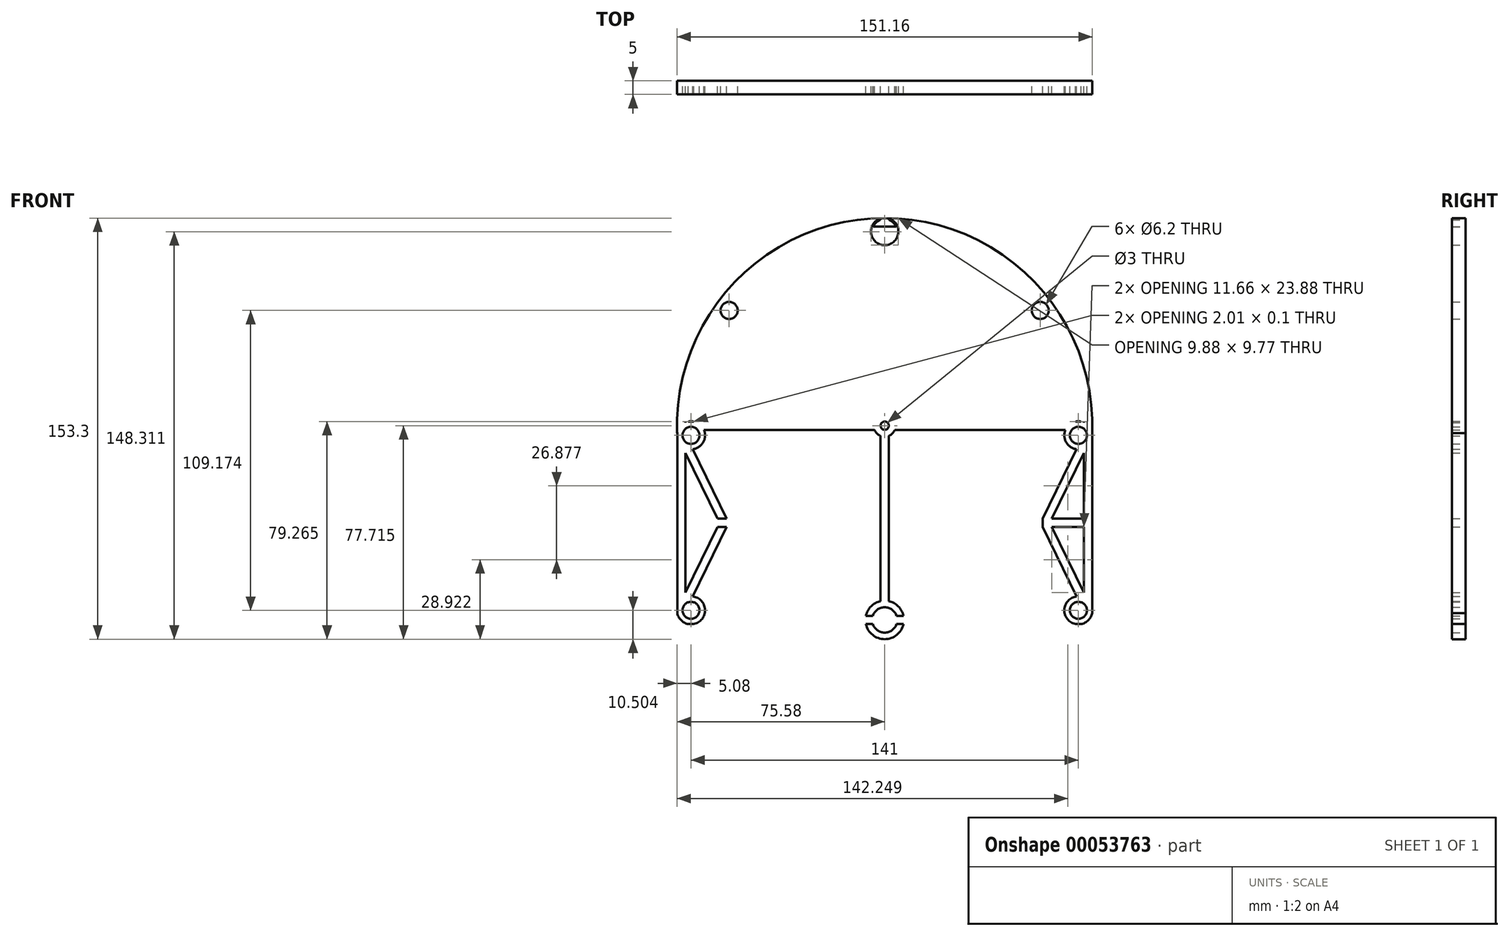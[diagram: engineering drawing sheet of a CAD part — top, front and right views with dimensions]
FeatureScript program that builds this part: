
annotation { "Feature Type Name" : "Feature", "Feature Type Description" : "" }
export const myFeature = defineFeature(function(context is Context, id is Id, definition is map)
    precondition{}
    {
        {
            var Q0;
            Q0=qCreatedBy(makeId("Front.planeOp"),FACE);
            var sketch = newSketch(context, id + "F0", { "sketchPlane" : qUnion([Q0])});
            skPoint(sketch, "E0", {"position": v(-3.58, 32.7) * mm});
            skPoint(sketch, "E1", {"position": v(-3.58, -38) * mm});
            skLineSegment(sketch, "E2.bottom", {"start": v(-5.08, 122.7) * mm, "end": v(-2.08, 122.7) * mm});
            skLineSegment(sketch, "E2.top", {"start": v(-5.08, -57.3) * mm, "end": v(-2.08, -57.3) * mm});
            skLineSegment(sketch, "E2.left", {"start": v(-5.08, 122.7) * mm, "end": v(-5.08, -57.3) * mm});
            skLineSegment(sketch, "E2.right", {"start": v(-2.08, 122.7) * mm, "end": v(-2.08, -57.3) * mm});
            skLineSegment(sketch, "E3", {"start": v(-3.58, 122.7) * mm, "end": v(-3.58, -57.3) * mm, "construction": true});
            skCircle(sketch, "E4", {"center": v(-3.58, 32.7) * mm, "radius": 1.5 * mm});
            skCircle(sketch, "E5", {"center": v(-3.58, -38) * mm, "radius": 1.5 * mm});
            skCircle(sketch, "E6", {"center": v(-3.58, 32.7) * mm, "radius": 4 * mm});
            skCircle(sketch, "E7", {"center": v(-3.58, -38) * mm, "radius": 7 * mm});
            skCircle(sketch, "E8", {"center": v(-3.58, 103.42) * mm, "radius": 4.5 * mm});
            skCircle(sketch, "E9", {"center": v(-3.58, 103.42) * mm, "radius": 5 * mm});
            skLineSegment(sketch, "E10.bottom", {"start": v(-76.08, -36.5) * mm, "end": v(68.92, -36.5) * mm});
            skLineSegment(sketch, "E10.top", {"start": v(-76.08, -39.5) * mm, "end": v(68.92, -39.5) * mm});
            skLineSegment(sketch, "E10.left", {"start": v(-76.08, -36.5) * mm, "end": v(-76.08, -39.5) * mm});
            skLineSegment(sketch, "E10.right", {"start": v(68.92, -36.5) * mm, "end": v(68.92, -39.5) * mm});
            skPoint(sketch, "E11", {"position": v(-3.58, -36.5) * mm});
            skPoint(sketch, "E12", {"position": v(-3.58, 34.2) * mm});
            skLineSegment(sketch, "E13.bottom", {"start": v(-76.08, 34.2) * mm, "end": v(68.92, 34.2) * mm});
            skLineSegment(sketch, "E13.top", {"start": v(-76.08, 31.2) * mm, "end": v(68.92, 31.2) * mm});
            skLineSegment(sketch, "E13.right", {"start": v(68.92, 34.2) * mm, "end": v(68.92, 31.2) * mm});
            skLineSegment(sketch, "E13.left", {"start": v(-76.08, 34.2) * mm, "end": v(-76.08, 31.2) * mm});
            skLineSegment(sketch, "E14.bottom", {"start": v(68.92, 34.2) * mm, "end": v(71.92, 34.2) * mm});
            skLineSegment(sketch, "E14.top", {"start": v(68.92, -39.5) * mm, "end": v(71.92, -39.5) * mm});
            skLineSegment(sketch, "E14.left", {"start": v(68.92, 34.2) * mm, "end": v(68.92, -39.5) * mm});
            skLineSegment(sketch, "E14.right", {"start": v(71.92, 34.2) * mm, "end": v(71.92, -39.5) * mm});
            skLineSegment(sketch, "E15.bottom", {"start": v(-76.08, 34.2) * mm, "end": v(-79.08, 34.2) * mm});
            skLineSegment(sketch, "E15.top", {"start": v(-76.08, -39.5) * mm, "end": v(-79.08, -39.5) * mm});
            skLineSegment(sketch, "E15.left", {"start": v(-76.08, 34.2) * mm, "end": v(-76.08, -39.5) * mm});
            skLineSegment(sketch, "E15.right", {"start": v(-79.08, 34.2) * mm, "end": v(-79.08, -39.5) * mm});
            skLineSegment(sketch, "E16", {"start": v(66.92, 34.2) * mm, "end": v(66.92, 29.2) * mm, "construction": true});
            skCircle(sketch, "E17", {"center": v(-3.58, -38) * mm, "radius": 64 * mm, "construction": true});
            skCircle(sketch, "E18", {"center": v(-3.58, 32.7) * mm, "radius": 64 * mm, "construction": true});
            skCircle(sketch, "E19", {"center": v(66.92, 29.2) * mm, "radius": 5.1 * mm});
            skCircle(sketch, "E20", {"center": v(66.92, 29.2) * mm, "radius": 3.1 * mm});
            skCircle(sketch, "E21", {"center": v(-3.58, -38) * mm, "radius": 4.6 * mm});
            skCircle(sketch, "E22.0.1.0", {"center": v(66.92, -34.5) * mm, "radius": 5.1 * mm});
            skCircle(sketch, "E22.0.1.2", {"center": v(66.92, -34.5) * mm, "radius": 3.1 * mm});
            skCircle(sketch, "E22.1.0.0", {"center": v(-74.08, 29.2) * mm, "radius": 5.1 * mm});
            skCircle(sketch, "E22.1.0.2", {"center": v(-74.08, 29.2) * mm, "radius": 3.1 * mm});
            skCircle(sketch, "E22.1.1.0", {"center": v(-74.08, -34.5) * mm, "radius": 5.1 * mm});
            skCircle(sketch, "E22.1.1.2", {"center": v(-74.08, -34.5) * mm, "radius": 3.1 * mm});
            skLineSegment(sketch, "E22.direction1", {"start": v(66.92, 29.2) * mm, "end": v(-74.08, 29.2) * mm, "construction": true});
            skLineSegment(sketch, "E22.direction2", {"start": v(66.92, 29.2) * mm, "end": v(66.92, -34.5) * mm, "construction": true});
            skArc(sketch, "E23", {"start": v(71.92, 29.2) * mm, "mid": v(-3.58, 108.29) * mm, "end": v(-79.08, 29.2) * mm});
            skArc(sketch, "E24", {"start": v(68.92, 33.79) * mm, "mid": v(-3.58, 105.21) * mm, "end": v(-76.08, 33.79) * mm});
            skLineSegment(sketch, "E25", {"start": v(-64.3, 77.7) * mm, "end": v(57.14, 77.7) * mm, "construction": true});
            skLineSegment(sketch, "E26", {"start": v(-64.3, 77.7) * mm, "end": v(-60.2, 74.67) * mm, "construction": true});
            skCircle(sketch, "E27", {"center": v(-60.2, 74.67) * mm, "radius": 5.1 * mm});
            skCircle(sketch, "E28", {"center": v(-60.2, 74.67) * mm, "radius": 3.1 * mm});
            skCircle(sketch, "E29.MirrorC", {"center": v(53.05, 74.67) * mm, "radius": 5.1 * mm});
            skCircle(sketch, "E30.MirrorC", {"center": v(53.05, 74.67) * mm, "radius": 3.1 * mm});
            skLineSegment(sketch, "E31", {"start": v(-79.08, -2.65) * mm, "end": v(71.92, -2.65) * mm, "construction": true});
            skLineSegment(sketch, "E32.bottom", {"start": v(-76.08, -1.15) * mm, "end": v(-61.08, -1.15) * mm});
            skLineSegment(sketch, "E32.top", {"start": v(-76.08, -4.15) * mm, "end": v(-61.08, -4.15) * mm});
            skLineSegment(sketch, "E32.left", {"start": v(-76.08, -1.15) * mm, "end": v(-76.08, -4.15) * mm});
            skLineSegment(sketch, "E32.right", {"start": v(-61.08, -1.15) * mm, "end": v(-61.08, -4.15) * mm});
            skPoint(sketch, "E33", {"position": v(-76.08, -2.65) * mm});
            skLineSegment(sketch, "E34", {"start": v(-61.08, -2.65) * mm, "end": v(-79.08, 34.2) * mm, "construction": true});
            skLineSegment(sketch, "E35", {"start": v(-61.08, -2.65) * mm, "end": v(-79.08, -39.5) * mm, "construction": true});
            skLineSegment(sketch, "E36", {"start": v(-61.08, -1.15) * mm, "end": v(-73.44, 24.15) * mm});
            skLineSegment(sketch, "E37", {"start": v(-76.08, 22.73) * mm, "end": v(-64.42, -1.15) * mm});
            skLineSegment(sketch, "E38", {"start": v(-61.08, -4.15) * mm, "end": v(-73.44, -29.45) * mm});
            skLineSegment(sketch, "E39", {"start": v(-64.42, -4.15) * mm, "end": v(-76.08, -28.03) * mm});
            skLineSegment(sketch, "E40.MirrorCS", {"start": v(68.92, -1.15) * mm, "end": v(53.92, -1.15) * mm});
            skLineSegment(sketch, "E41.MirrorCS", {"start": v(68.92, -4.15) * mm, "end": v(53.92, -4.15) * mm});
            skLineSegment(sketch, "E42.MirrorCS", {"start": v(53.92, -1.15) * mm, "end": v(53.92, -4.15) * mm});
            skLineSegment(sketch, "E43.MirrorCS", {"start": v(53.92, -1.15) * mm, "end": v(66.27, 24.15) * mm});
            skLineSegment(sketch, "E44.MirrorCS", {"start": v(68.92, 22.73) * mm, "end": v(57.26, -1.15) * mm});
            skLineSegment(sketch, "E45.MirrorCS", {"start": v(53.92, -4.15) * mm, "end": v(66.27, -29.45) * mm});
            skLineSegment(sketch, "E46.MirrorCS", {"start": v(57.26, -4.15) * mm, "end": v(68.92, -28.03) * mm});
            skSolve(sketch);
        }
        {
            var Q0;
            {var subQ0=sQuery(id+"F0.wireOp",EDGE,"E4");var subQ1=sQuery(id+"F0.wireOp",EDGE,"E2.left");var subQ2=makeQuery(id+"F0.imprint","INTERSECT",VERTEX,{"derivedFrom":[subQ1,subQ0]});Q0=makeQuery(id+"F0.imprint","IMPRINT",FACE,{"disambiguationData":[TD([[makeQuery(id+"F0.imprint","IMPRINT",EDGE,{"disambiguationData":[TD([[subQ2,-1.0]])],"derivedFrom":subQ1}),1.0]])]});}
            var Q1;
            {var subQ0=sQuery(id+"F0.wireOp",EDGE,"E4");var subQ1=sQuery(id+"F0.wireOp",EDGE,"E2.right");var subQ2=makeQuery(id+"F0.imprint","INTERSECT",VERTEX,{"derivedFrom":[subQ1,subQ0]});Q1=makeQuery(id+"F0.imprint","IMPRINT",FACE,{"disambiguationData":[TD([[makeQuery(id+"F0.imprint","IMPRINT",EDGE,{"disambiguationData":[TD([[subQ2,-1.0]])],"derivedFrom":subQ1}),-1.0]])]});}
            var Q2;
            {var subQ0=sQuery(id+"F0.wireOp",EDGE,"E13.bottom");var subQ3=sQuery(id+"F0.wireOp",EDGE,"E2.left");var subQ4=makeQuery(id+"F0.imprint","INTERSECT",VERTEX,{"derivedFrom":[subQ3,subQ0]});Q2=makeQuery(id+"F0.imprint","IMPRINT",FACE,{"disambiguationData":[TD([[makeQuery(id+"F0.imprint","IMPRINT",EDGE,{"disambiguationData":[TD([[subQ4,-1.0]])],"derivedFrom":subQ3}),-1.0]])]});}
            var Q3;
            {var subQ0=sQuery(id+"F0.wireOp",EDGE,"E13.bottom");var subQ3=sQuery(id+"F0.wireOp",EDGE,"E2.right");var subQ4=makeQuery(id+"F0.imprint","INTERSECT",VERTEX,{"derivedFrom":[subQ3,subQ0]});Q3=makeQuery(id+"F0.imprint","IMPRINT",FACE,{"disambiguationData":[TD([[makeQuery(id+"F0.imprint","IMPRINT",EDGE,{"disambiguationData":[TD([[subQ4,-1.0]])],"derivedFrom":subQ3}),1.0]])]});}
            var Q4;
            {var subQ0=sQuery(id+"F0.wireOp",EDGE,"E13.bottom");var subQ1=sQuery(id+"F0.wireOp",EDGE,"E2.right");var subQ2=makeQuery(id+"F0.imprint","INTERSECT",VERTEX,{"derivedFrom":[subQ1,subQ0]});Q4=makeQuery(id+"F0.imprint","IMPRINT",FACE,{"disambiguationData":[TD([[makeQuery(id+"F0.imprint","IMPRINT",EDGE,{"disambiguationData":[TD([[subQ2,-1.0]])],"derivedFrom":subQ1}),-1.0]])]});}
            var Q5;
            {var subQ0=sQuery(id+"F0.wireOp",EDGE,"E13.bottom");var subQ1=sQuery(id+"F0.wireOp",EDGE,"E2.left");var subQ2=makeQuery(id+"F0.imprint","INTERSECT",VERTEX,{"derivedFrom":[subQ1,subQ0]});Q5=makeQuery(id+"F0.imprint","IMPRINT",FACE,{"disambiguationData":[TD([[makeQuery(id+"F0.imprint","IMPRINT",EDGE,{"disambiguationData":[TD([[subQ2,-1.0]])],"derivedFrom":subQ1}),1.0]])]});}
            var Q6;
            {var subQ0=sQuery(id+"F0.wireOp",EDGE,"E13.top");var subQ1=sQuery(id+"F0.wireOp",EDGE,"E2.left");var subQ2=makeQuery(id+"F0.imprint","INTERSECT",VERTEX,{"derivedFrom":[subQ1,subQ0]});Q6=makeQuery(id+"F0.imprint","IMPRINT",FACE,{"disambiguationData":[TD([[makeQuery(id+"F0.imprint","IMPRINT",EDGE,{"disambiguationData":[TD([[subQ2,-1.0]])],"derivedFrom":subQ1}),1.0]])]});}
            var Q7;
            {var subQ0=sQuery(id+"F0.wireOp",EDGE,"E13.top");var subQ1=sQuery(id+"F0.wireOp",EDGE,"E2.left");var subQ2=makeQuery(id+"F0.imprint","INTERSECT",VERTEX,{"derivedFrom":[subQ1,subQ0]});Q7=makeQuery(id+"F0.imprint","IMPRINT",FACE,{"disambiguationData":[TD([[makeQuery(id+"F0.imprint","IMPRINT",EDGE,{"disambiguationData":[TD([[subQ2,-1.0]])],"derivedFrom":subQ1}),1.0]])]});}
            var Q8;
            {var subQ0=sQuery(id+"F0.wireOp",EDGE,"E22.1.0.2");var subQ1=sQuery(id+"F0.wireOp",EDGE,"E15.left");var subQ2=makeQuery(id+"F0.imprint","INTERSECT",VERTEX,{"disambiguationData":[OD(1.0)],"derivedFrom":[subQ1,subQ0]});Q8=makeQuery(id+"F0.imprint","IMPRINT",FACE,{"disambiguationData":[TD([[makeQuery(id+"F0.imprint","IMPRINT",EDGE,{"disambiguationData":[TD([[subQ2,-1.0]])],"derivedFrom":subQ1}),-1.0]])]});}
            var Q9;
            {var subQ0=sQuery(id+"F0.wireOp",EDGE,"E19");var subQ1=sQuery(id+"F0.wireOp",EDGE,"E14.left");var subQ2=makeQuery(id+"F0.imprint","INTERSECT",VERTEX,{"derivedFrom":[subQ1,subQ0]});Q9=makeQuery(id+"F0.imprint","IMPRINT",FACE,{"disambiguationData":[TD([[makeQuery(id+"F0.imprint","IMPRINT",EDGE,{"disambiguationData":[TD([[subQ2,-1.0]])],"derivedFrom":subQ1}),1.0]])]});}
            var Q10;
            {var subQ0=sQuery(id+"F0.wireOp",EDGE,"E19");var subQ1=sQuery(id+"F0.wireOp",EDGE,"E14.left");var subQ2=makeQuery(id+"F0.imprint","INTERSECT",VERTEX,{"derivedFrom":[subQ1,subQ0]});Q10=makeQuery(id+"F0.imprint","IMPRINT",FACE,{"disambiguationData":[TD([[makeQuery(id+"F0.imprint","IMPRINT",EDGE,{"disambiguationData":[TD([[subQ2,-1.0]])],"derivedFrom":subQ1}),1.0]])]});}
            var Q11;
            {var subQ0=sQuery(id+"F0.wireOp",EDGE,"E19");var subQ1=sQuery(id+"F0.wireOp",EDGE,"E13.top");var subQ2=makeQuery(id+"F0.imprint","INTERSECT",VERTEX,{"derivedFrom":[subQ1,subQ0]});Q11=makeQuery(id+"F0.imprint","IMPRINT",FACE,{"disambiguationData":[TD([[makeQuery(id+"F0.imprint","IMPRINT",EDGE,{"disambiguationData":[TD([[subQ2,-1.0]])],"derivedFrom":subQ1}),-1.0]])]});}
            var Q12;
            {var subQ0=sQuery(id+"F0.wireOp",EDGE,"E19");var subQ3=sQuery(id+"F0.wireOp",EDGE,"E13.top");var subQ4=makeQuery(id+"F0.imprint","INTERSECT",VERTEX,{"derivedFrom":[subQ3,subQ0]});Q12=makeQuery(id+"F0.imprint","IMPRINT",FACE,{"disambiguationData":[TD([[makeQuery(id+"F0.imprint","IMPRINT",EDGE,{"disambiguationData":[TD([[subQ4,-1.0]])],"derivedFrom":subQ3}),1.0]])]});}
            var Q13;
            {var subQ0=sQuery(id+"F0.wireOp",EDGE,"E13.bottom");var subQ1=sQuery(id+"F0.wireOp",EDGE,"E6");var subQ2=makeQuery(id+"F0.imprint","INTERSECT",VERTEX,{"disambiguationData":[OD(1.0)],"derivedFrom":[subQ1,subQ0]});Q13=makeQuery(id+"F0.imprint","IMPRINT",FACE,{"disambiguationData":[TD([[makeQuery(id+"F0.imprint","IMPRINT",EDGE,{"disambiguationData":[TD([[subQ2,-1.0]])],"derivedFrom":subQ1}),-1.0]])]});}
            var Q14;
            {var subQ0=sQuery(id+"F0.wireOp",EDGE,"E13.bottom");var subQ1=sQuery(id+"F0.wireOp",EDGE,"E6");var subQ2=makeQuery(id+"F0.imprint","INTERSECT",VERTEX,{"disambiguationData":[OD(0.0)],"derivedFrom":[subQ1,subQ0]});Q14=makeQuery(id+"F0.imprint","IMPRINT",FACE,{"disambiguationData":[TD([[makeQuery(id+"F0.imprint","IMPRINT",EDGE,{"disambiguationData":[TD([[subQ2,1.0]])],"derivedFrom":subQ1}),-1.0]])]});}
            var Q15;
            {var subQ0=sQuery(id+"F0.wireOp",EDGE,"E10.top");var subQ1=sQuery(id+"F0.wireOp",EDGE,"E7");var subQ2=makeQuery(id+"F0.imprint","INTERSECT",VERTEX,{"disambiguationData":[OD(1.0)],"derivedFrom":[subQ1,subQ0]});Q15=makeQuery(id+"F0.imprint","IMPRINT",FACE,{"disambiguationData":[TD([[makeQuery(id+"F0.imprint","IMPRINT",EDGE,{"disambiguationData":[TD([[subQ2,-1.0]])],"derivedFrom":subQ1}),-1.0]])]});}
            var Q16;
            {var subQ0=sQuery(id+"F0.wireOp",EDGE,"E10.top");var subQ1=sQuery(id+"F0.wireOp",EDGE,"E7");var subQ2=makeQuery(id+"F0.imprint","INTERSECT",VERTEX,{"disambiguationData":[OD(0.0)],"derivedFrom":[subQ1,subQ0]});Q16=makeQuery(id+"F0.imprint","IMPRINT",FACE,{"disambiguationData":[TD([[makeQuery(id+"F0.imprint","IMPRINT",EDGE,{"disambiguationData":[TD([[subQ2,1.0]])],"derivedFrom":subQ1}),-1.0]])]});}
            var Q17;
            {var subQ0=sQuery(id+"F0.wireOp",EDGE,"E13.top");var subQ1=sQuery(id+"F0.wireOp",EDGE,"E2.right");var subQ2=makeQuery(id+"F0.imprint","INTERSECT",VERTEX,{"derivedFrom":[subQ1,subQ0]});Q17=makeQuery(id+"F0.imprint","IMPRINT",FACE,{"disambiguationData":[TD([[makeQuery(id+"F0.imprint","IMPRINT",EDGE,{"disambiguationData":[TD([[subQ2,-1.0]])],"derivedFrom":subQ1}),1.0]])]});}
            var Q18;
            {var subQ0=sQuery(id+"F0.wireOp",EDGE,"E13.top");var subQ1=sQuery(id+"F0.wireOp",EDGE,"E2.left");var subQ2=makeQuery(id+"F0.imprint","INTERSECT",VERTEX,{"derivedFrom":[subQ1,subQ0]});Q18=makeQuery(id+"F0.imprint","IMPRINT",FACE,{"disambiguationData":[TD([[makeQuery(id+"F0.imprint","IMPRINT",EDGE,{"disambiguationData":[TD([[subQ2,-1.0]])],"derivedFrom":subQ1}),-1.0]])]});}
            var Q19;
            {var subQ1=sQuery(id+"F0.wireOp",EDGE,"E2.left");var subQ4=sQuery(id+"F0.wireOp",EDGE,"E6");var subQ5=makeQuery(id+"F0.imprint","INTERSECT",VERTEX,{"disambiguationData":[OD(0.0)],"derivedFrom":[subQ1,subQ4]});Q19=makeQuery(id+"F0.imprint","IMPRINT",FACE,{"disambiguationData":[TD([[makeQuery(id+"F0.imprint","IMPRINT",EDGE,{"disambiguationData":[TD([[subQ5,-1.0]])],"derivedFrom":subQ1}),1.0]])]});}
            var Q20;
            {var subQ0=sQuery(id+"F0.wireOp",EDGE,"E6");var subQ1=sQuery(id+"F0.wireOp",EDGE,"E2.right");var subQ2=makeQuery(id+"F0.imprint","INTERSECT",VERTEX,{"disambiguationData":[OD(0.0)],"derivedFrom":[subQ1,subQ0]});Q20=makeQuery(id+"F0.imprint","IMPRINT",FACE,{"disambiguationData":[TD([[makeQuery(id+"F0.imprint","IMPRINT",EDGE,{"disambiguationData":[TD([[subQ2,-1.0]])],"derivedFrom":subQ1}),1.0]])]});}
            var Q21;
            {var subQ0=sQuery(id+"F0.wireOp",EDGE,"E6");var subQ1=sQuery(id+"F0.wireOp",EDGE,"E2.left");var subQ2=makeQuery(id+"F0.imprint","INTERSECT",VERTEX,{"disambiguationData":[OD(0.0)],"derivedFrom":[subQ1,subQ0]});Q21=makeQuery(id+"F0.imprint","IMPRINT",FACE,{"disambiguationData":[TD([[makeQuery(id+"F0.imprint","IMPRINT",EDGE,{"disambiguationData":[TD([[subQ2,-1.0]])],"derivedFrom":subQ1}),-1.0]])]});}
            var Q22;
            {var subQ0=sQuery(id+"F0.wireOp",EDGE,"E4");var subQ1=sQuery(id+"F0.wireOp",EDGE,"E2.right");var subQ2=makeQuery(id+"F0.imprint","INTERSECT",VERTEX,{"derivedFrom":[subQ1,subQ0]});Q22=makeQuery(id+"F0.imprint","IMPRINT",FACE,{"disambiguationData":[TD([[makeQuery(id+"F0.imprint","IMPRINT",EDGE,{"disambiguationData":[TD([[subQ2,-1.0]])],"derivedFrom":subQ1}),-1.0]])]});}
            var Q23;
            {var subQ0=sQuery(id+"F0.wireOp",EDGE,"E4");var subQ1=sQuery(id+"F0.wireOp",EDGE,"E2.left");var subQ2=makeQuery(id+"F0.imprint","INTERSECT",VERTEX,{"derivedFrom":[subQ1,subQ0]});Q23=makeQuery(id+"F0.imprint","IMPRINT",FACE,{"disambiguationData":[TD([[makeQuery(id+"F0.imprint","IMPRINT",EDGE,{"disambiguationData":[TD([[subQ2,-1.0]])],"derivedFrom":subQ1}),1.0]])]});}
            var Q24;
            {var subQ0=sQuery(id+"F0.wireOp",EDGE,"E7");var subQ1=sQuery(id+"F0.wireOp",EDGE,"E2.left");var subQ2=makeQuery(id+"F0.imprint","INTERSECT",VERTEX,{"disambiguationData":[OD(0.0)],"derivedFrom":[subQ1,subQ0]});Q24=makeQuery(id+"F0.imprint","IMPRINT",FACE,{"disambiguationData":[TD([[makeQuery(id+"F0.imprint","IMPRINT",EDGE,{"disambiguationData":[TD([[subQ2,1.0]])],"derivedFrom":subQ1}),1.0]])]});}
            var Q25;
            {var subQ0=sQuery(id+"F0.wireOp",EDGE,"E7");var subQ1=sQuery(id+"F0.wireOp",EDGE,"E2.right");var subQ2=makeQuery(id+"F0.imprint","INTERSECT",VERTEX,{"disambiguationData":[OD(0.0)],"derivedFrom":[subQ1,subQ0]});Q25=makeQuery(id+"F0.imprint","IMPRINT",FACE,{"disambiguationData":[TD([[makeQuery(id+"F0.imprint","IMPRINT",EDGE,{"disambiguationData":[TD([[subQ2,1.0]])],"derivedFrom":subQ1}),1.0]])]});}
            var Q26;
            {var subQ0=sQuery(id+"F0.wireOp",EDGE,"E7");var subQ1=sQuery(id+"F0.wireOp",EDGE,"E2.left");var subQ2=makeQuery(id+"F0.imprint","INTERSECT",VERTEX,{"disambiguationData":[OD(0.0)],"derivedFrom":[subQ1,subQ0]});Q26=makeQuery(id+"F0.imprint","IMPRINT",FACE,{"disambiguationData":[TD([[makeQuery(id+"F0.imprint","IMPRINT",EDGE,{"disambiguationData":[TD([[subQ2,1.0]])],"derivedFrom":subQ1}),-1.0]])]});}
            var Q27;
            {var subQ0=sQuery(id+"F0.wireOp",EDGE,"E7");var subQ1=sQuery(id+"F0.wireOp",EDGE,"E2.left");var subQ2=makeQuery(id+"F0.imprint","INTERSECT",VERTEX,{"disambiguationData":[OD(1.0)],"derivedFrom":[subQ1,subQ0]});Q27=makeQuery(id+"F0.imprint","IMPRINT",FACE,{"disambiguationData":[TD([[makeQuery(id+"F0.imprint","IMPRINT",EDGE,{"disambiguationData":[TD([[subQ2,-1.0]])],"derivedFrom":subQ1}),-1.0]])]});}
            var Q28;
            {var subQ0=sQuery(id+"F0.wireOp",EDGE,"E7");var subQ1=sQuery(id+"F0.wireOp",EDGE,"E2.left");var subQ2=makeQuery(id+"F0.imprint","INTERSECT",VERTEX,{"disambiguationData":[OD(1.0)],"derivedFrom":[subQ1,subQ0]});Q28=makeQuery(id+"F0.imprint","IMPRINT",FACE,{"disambiguationData":[TD([[makeQuery(id+"F0.imprint","IMPRINT",EDGE,{"disambiguationData":[TD([[subQ2,-1.0]])],"derivedFrom":subQ1}),1.0]])]});}
            var Q29;
            {var subQ0=sQuery(id+"F0.wireOp",EDGE,"E7");var subQ1=sQuery(id+"F0.wireOp",EDGE,"E2.right");var subQ2=makeQuery(id+"F0.imprint","INTERSECT",VERTEX,{"disambiguationData":[OD(1.0)],"derivedFrom":[subQ1,subQ0]});Q29=makeQuery(id+"F0.imprint","IMPRINT",FACE,{"disambiguationData":[TD([[makeQuery(id+"F0.imprint","IMPRINT",EDGE,{"disambiguationData":[TD([[subQ2,-1.0]])],"derivedFrom":subQ1}),1.0]])]});}
            var Q30;
            {var subQ0=sQuery(id+"F0.wireOp",EDGE,"E10.top");var subQ1=sQuery(id+"F0.wireOp",EDGE,"E7");var subQ2=makeQuery(id+"F0.imprint","INTERSECT",VERTEX,{"disambiguationData":[OD(1.0)],"derivedFrom":[subQ1,subQ0]});Q30=makeQuery(id+"F0.imprint","IMPRINT",FACE,{"disambiguationData":[TD([[makeQuery(id+"F0.imprint","IMPRINT",EDGE,{"disambiguationData":[TD([[subQ2,-1.0]])],"derivedFrom":subQ1}),1.0]])]});}
            var Q31;
            {var subQ0=sQuery(id+"F0.wireOp",EDGE,"E10.top");var subQ1=sQuery(id+"F0.wireOp",EDGE,"E7");var subQ2=makeQuery(id+"F0.imprint","INTERSECT",VERTEX,{"disambiguationData":[OD(0.0)],"derivedFrom":[subQ1,subQ0]});Q31=makeQuery(id+"F0.imprint","IMPRINT",FACE,{"disambiguationData":[TD([[makeQuery(id+"F0.imprint","IMPRINT",EDGE,{"disambiguationData":[TD([[subQ2,1.0]])],"derivedFrom":subQ1}),1.0]])]});}
            var Q32;
            {var subQ4=sQuery(id+"F0.wireOp",EDGE,"E20");var subQ5=sQuery(id+"F0.wireOp",EDGE,"E14.left");var subQ6=makeQuery(id+"F0.imprint","INTERSECT",VERTEX,{"disambiguationData":[OD(1.0)],"derivedFrom":[subQ5,subQ4]});Q32=makeQuery(id+"F0.imprint","IMPRINT",FACE,{"disambiguationData":[TD([[makeQuery(id+"F0.imprint","IMPRINT",EDGE,{"disambiguationData":[TD([[subQ6,-1.0]])],"derivedFrom":subQ5}),1.0]])]});}
            var Q33;
            {var subQ0=sQuery(id+"F0.wireOp",EDGE,"E22.0.1.0");var subQ3=sQuery(id+"F0.wireOp",EDGE,"E10.bottom");var subQ4=makeQuery(id+"F0.imprint","INTERSECT",VERTEX,{"derivedFrom":[subQ3,subQ0]});Q33=makeQuery(id+"F0.imprint","IMPRINT",FACE,{"disambiguationData":[TD([[makeQuery(id+"F0.imprint","IMPRINT",EDGE,{"disambiguationData":[TD([[subQ4,-1.0]])],"derivedFrom":subQ3}),-1.0]])]});}
            var Q34;
            {var subQ0=sQuery(id+"F0.wireOp",EDGE,"E22.0.1.0");var subQ1=sQuery(id+"F0.wireOp",EDGE,"E10.bottom");var subQ2=makeQuery(id+"F0.imprint","INTERSECT",VERTEX,{"derivedFrom":[subQ1,subQ0]});Q34=makeQuery(id+"F0.imprint","IMPRINT",FACE,{"disambiguationData":[TD([[makeQuery(id+"F0.imprint","IMPRINT",EDGE,{"disambiguationData":[TD([[subQ2,-1.0]])],"derivedFrom":subQ1}),1.0]])]});}
            var Q35;
            {var subQ0=sQuery(id+"F0.wireOp",EDGE,"E22.1.0.0");var subQ1=sQuery(id+"F0.wireOp",EDGE,"E15.left");var subQ2=makeQuery(id+"F0.imprint","INTERSECT",VERTEX,{"derivedFrom":[subQ1,subQ0]});Q35=makeQuery(id+"F0.imprint","IMPRINT",FACE,{"disambiguationData":[TD([[makeQuery(id+"F0.imprint","IMPRINT",EDGE,{"disambiguationData":[TD([[subQ2,-1.0]])],"derivedFrom":subQ1}),-1.0]])]});}
            var Q36;
            {var subQ3=sQuery(id+"F0.wireOp",EDGE,"E13.top");var subQ5=sQuery(id+"F0.wireOp",EDGE,"E22.1.0.2");var subQ6=makeQuery(id+"F0.imprint","INTERSECT",VERTEX,{"derivedFrom":[subQ3,subQ5]});Q36=makeQuery(id+"F0.imprint","IMPRINT",FACE,{"disambiguationData":[TD([[makeQuery(id+"F0.imprint","IMPRINT",EDGE,{"disambiguationData":[TD([[subQ6,-1.0]])],"derivedFrom":subQ3}),1.0]])]});}
            var Q37;
            {var subQ0=sQuery(id+"F0.wireOp",EDGE,"E22.1.0.2");var subQ1=sQuery(id+"F0.wireOp",EDGE,"E13.top");var subQ2=makeQuery(id+"F0.imprint","INTERSECT",VERTEX,{"derivedFrom":[subQ1,subQ0]});Q37=makeQuery(id+"F0.imprint","IMPRINT",FACE,{"disambiguationData":[TD([[makeQuery(id+"F0.imprint","IMPRINT",EDGE,{"disambiguationData":[TD([[subQ2,-1.0]])],"derivedFrom":subQ1}),-1.0]])]});}
            var Q38;
            {var subQ0=sQuery(id+"F0.wireOp",EDGE,"E22.1.1.2");var subQ1=sQuery(id+"F0.wireOp",EDGE,"E10.bottom");var subQ2=makeQuery(id+"F0.imprint","INTERSECT",VERTEX,{"derivedFrom":[subQ1,subQ0]});Q38=makeQuery(id+"F0.imprint","IMPRINT",FACE,{"disambiguationData":[TD([[makeQuery(id+"F0.imprint","IMPRINT",EDGE,{"disambiguationData":[TD([[subQ2,-1.0]])],"derivedFrom":subQ1}),1.0]])]});}
            var Q39;
            {var subQ5=sQuery(id+"F0.wireOp",EDGE,"E22.1.1.2");var subQ7=sQuery(id+"F0.wireOp",EDGE,"E10.bottom");var subQ9=makeQuery(id+"F0.imprint","INTERSECT",VERTEX,{"derivedFrom":[subQ7,subQ5]});Q39=makeQuery(id+"F0.imprint","IMPRINT",FACE,{"disambiguationData":[TD([[makeQuery(id+"F0.imprint","IMPRINT",EDGE,{"disambiguationData":[TD([[subQ9,-1.0]])],"derivedFrom":subQ7}),-1.0]])]});}
            var Q40;
            {var subQ0=sQuery(id+"F0.wireOp",EDGE,"E22.0.1.0");var subQ2=sQuery(id+"F0.wireOp",EDGE,"E14.left");var subQ4=makeQuery(id+"F0.imprint","INTERSECT",VERTEX,{"disambiguationData":[OD(0.0)],"derivedFrom":[subQ2,subQ0]});Q40=makeQuery(id+"F0.imprint","IMPRINT",FACE,{"disambiguationData":[TD([[makeQuery(id+"F0.imprint","IMPRINT",EDGE,{"disambiguationData":[TD([[subQ4,-1.0]])],"derivedFrom":subQ2}),1.0]])]});}
            var Q41;
            {var subQ0=sQuery(id+"F0.wireOp",EDGE,"E22.1.1.0");var subQ2=sQuery(id+"F0.wireOp",EDGE,"E15.left");var subQ4=makeQuery(id+"F0.imprint","INTERSECT",VERTEX,{"disambiguationData":[OD(0.0)],"derivedFrom":[subQ2,subQ0]});Q41=makeQuery(id+"F0.imprint","IMPRINT",FACE,{"disambiguationData":[TD([[makeQuery(id+"F0.imprint","IMPRINT",EDGE,{"disambiguationData":[TD([[subQ4,-1.0]])],"derivedFrom":subQ2}),-1.0]])]});}
            var Q42;
            {var subQ0=sQuery(id+"F0.wireOp",EDGE,"E15.bottom");Q42=makeQuery(id+"F0.imprint","IMPRINT",FACE,{"disambiguationData":[TD([[makeQuery(id+"F0.imprint","IMPRINT",EDGE,{"derivedFrom":subQ0}),-1.0]])]});}
            var Q43;
            {var subQ0=sQuery(id+"F0.wireOp",EDGE,"E14.bottom");Q43=makeQuery(id+"F0.imprint","IMPRINT",FACE,{"disambiguationData":[TD([[makeQuery(id+"F0.imprint","IMPRINT",EDGE,{"derivedFrom":subQ0}),1.0]])]});}
            var Q44;
            {var subQ0=sQuery(id+"F0.wireOp",EDGE,"E15.bottom");Q44=makeQuery(id+"F0.imprint","IMPRINT",FACE,{"disambiguationData":[TD([[makeQuery(id+"F0.imprint","IMPRINT",EDGE,{"derivedFrom":subQ0}),1.0]])]});}
            var Q45;
            {var subQ0=sQuery(id+"F0.wireOp",EDGE,"E14.bottom");Q45=makeQuery(id+"F0.imprint","IMPRINT",FACE,{"disambiguationData":[TD([[makeQuery(id+"F0.imprint","IMPRINT",EDGE,{"derivedFrom":subQ0}),-1.0]])]});}
            var Q46;
            {var subQ0=sQuery(id+"F0.wireOp",EDGE,"E9");var subQ1=sQuery(id+"F0.wireOp",EDGE,"E2.left");var subQ2=makeQuery(id+"F0.imprint","INTERSECT",VERTEX,{"disambiguationData":[OD(0.0)],"derivedFrom":[subQ1,subQ0]});Q46=makeQuery(id+"F0.imprint","IMPRINT",FACE,{"disambiguationData":[TD([[makeQuery(id+"F0.imprint","IMPRINT",EDGE,{"disambiguationData":[TD([[subQ2,-1.0]])],"derivedFrom":subQ1}),-1.0]])]});}
            var Q47;
            {var subQ0=sQuery(id+"F0.wireOp",EDGE,"E9");var subQ8=sQuery(id+"F0.wireOp",EDGE,"E2.left");var subQ10=makeQuery(id+"F0.imprint","INTERSECT",VERTEX,{"disambiguationData":[OD(0.0)],"derivedFrom":[subQ8,subQ0]});Q47=makeQuery(id+"F0.imprint","IMPRINT",FACE,{"disambiguationData":[TD([[makeQuery(id+"F0.imprint","IMPRINT",EDGE,{"disambiguationData":[TD([[subQ10,-1.0]])],"derivedFrom":subQ8}),1.0]])]});}
            var Q48;
            {var subQ0=sQuery(id+"F0.wireOp",EDGE,"E9");var subQ1=sQuery(id+"F0.wireOp",EDGE,"E2.right");var subQ2=makeQuery(id+"F0.imprint","INTERSECT",VERTEX,{"disambiguationData":[OD(0.0)],"derivedFrom":[subQ1,subQ0]});Q48=makeQuery(id+"F0.imprint","IMPRINT",FACE,{"disambiguationData":[TD([[makeQuery(id+"F0.imprint","IMPRINT",EDGE,{"disambiguationData":[TD([[subQ2,-1.0]])],"derivedFrom":subQ1}),1.0]])]});}
            var Q49;
            {var subQ0=sQuery(id+"F0.wireOp",EDGE,"E8");var subQ1=sQuery(id+"F0.wireOp",EDGE,"E2.right");var subQ2=makeQuery(id+"F0.imprint","INTERSECT",VERTEX,{"disambiguationData":[OD(1.0)],"derivedFrom":[subQ1,subQ0]});Q49=makeQuery(id+"F0.imprint","IMPRINT",FACE,{"disambiguationData":[TD([[makeQuery(id+"F0.imprint","IMPRINT",EDGE,{"disambiguationData":[TD([[subQ2,-1.0]])],"derivedFrom":subQ1}),1.0]])]});}
            var Q50;
            {var subQ0=sQuery(id+"F0.wireOp",EDGE,"E8");var subQ1=sQuery(id+"F0.wireOp",EDGE,"E2.left");var subQ2=makeQuery(id+"F0.imprint","INTERSECT",VERTEX,{"disambiguationData":[OD(1.0)],"derivedFrom":[subQ1,subQ0]});Q50=makeQuery(id+"F0.imprint","IMPRINT",FACE,{"disambiguationData":[TD([[makeQuery(id+"F0.imprint","IMPRINT",EDGE,{"disambiguationData":[TD([[subQ2,-1.0]])],"derivedFrom":subQ1}),1.0]])]});}
            var Q51;
            {var subQ0=sQuery(id+"F0.wireOp",EDGE,"E8");var subQ1=sQuery(id+"F0.wireOp",EDGE,"E2.left");var subQ2=makeQuery(id+"F0.imprint","INTERSECT",VERTEX,{"disambiguationData":[OD(1.0)],"derivedFrom":[subQ1,subQ0]});Q51=makeQuery(id+"F0.imprint","IMPRINT",FACE,{"disambiguationData":[TD([[makeQuery(id+"F0.imprint","IMPRINT",EDGE,{"disambiguationData":[TD([[subQ2,-1.0]])],"derivedFrom":subQ1}),-1.0]])]});}
            var Q52;
            {var subQ0=sQuery(id+"F0.wireOp",EDGE,"E23");var subQ1=sQuery(id+"F0.wireOp",EDGE,"E2.right");var subQ2=makeQuery(id+"F0.imprint","INTERSECT",VERTEX,{"derivedFrom":[subQ1,subQ0]});Q52=makeQuery(id+"F0.imprint","IMPRINT",FACE,{"disambiguationData":[TD([[makeQuery(id+"F0.imprint","IMPRINT",EDGE,{"disambiguationData":[TD([[subQ2,-1.0]])],"derivedFrom":subQ1}),-1.0]])]});}
            var Q53;
            {var subQ0=sQuery(id+"F0.wireOp",EDGE,"E23");var subQ1=sQuery(id+"F0.wireOp",EDGE,"E2.left");var subQ2=makeQuery(id+"F0.imprint","INTERSECT",VERTEX,{"derivedFrom":[subQ1,subQ0]});Q53=makeQuery(id+"F0.imprint","IMPRINT",FACE,{"disambiguationData":[TD([[makeQuery(id+"F0.imprint","IMPRINT",EDGE,{"disambiguationData":[TD([[subQ2,-1.0]])],"derivedFrom":subQ1}),1.0]])]});}
            var Q54;
            {var subQ5=sQuery(id+"F0.wireOp",EDGE,"E23");var subQ6=sQuery(id+"F0.wireOp",EDGE,"E2.left");var subQ7=makeQuery(id+"F0.imprint","INTERSECT",VERTEX,{"derivedFrom":[subQ6,subQ5]});Q54=makeQuery(id+"F0.imprint","IMPRINT",FACE,{"disambiguationData":[TD([[makeQuery(id+"F0.imprint","IMPRINT",EDGE,{"disambiguationData":[TD([[subQ7,-1.0]])],"derivedFrom":subQ6}),-1.0]])]});}
            var Q55;
            {var subQ0=sQuery(id+"F0.wireOp",EDGE,"E27");var subQ2=sQuery(id+"F0.wireOp",EDGE,"E24");var subQ4=makeQuery(id+"F0.imprint","INTERSECT",VERTEX,{"disambiguationData":[OD(0.0)],"derivedFrom":[subQ2,subQ0]});Q55=makeQuery(id+"F0.imprint","IMPRINT",FACE,{"disambiguationData":[TD([[makeQuery(id+"F0.imprint","IMPRINT",EDGE,{"disambiguationData":[TD([[subQ4,-1.0]])],"derivedFrom":subQ2}),-1.0]])]});}
            var Q56;
            {var subQ0=sQuery(id+"F0.wireOp",EDGE,"E27");var subQ1=sQuery(id+"F0.wireOp",EDGE,"E24");var subQ2=makeQuery(id+"F0.imprint","INTERSECT",VERTEX,{"disambiguationData":[OD(0.0)],"derivedFrom":[subQ1,subQ0]});Q56=makeQuery(id+"F0.imprint","IMPRINT",FACE,{"disambiguationData":[TD([[makeQuery(id+"F0.imprint","IMPRINT",EDGE,{"disambiguationData":[TD([[subQ2,-1.0]])],"derivedFrom":subQ1}),1.0]])]});}
            var Q57;
            {var subQ0=sQuery(id+"F0.wireOp",EDGE,"E23");var subQ1=sQuery(id+"F0.wireOp",EDGE,"E2.right");var subQ2=makeQuery(id+"F0.imprint","INTERSECT",VERTEX,{"derivedFrom":[subQ1,subQ0]});Q57=makeQuery(id+"F0.imprint","IMPRINT",FACE,{"disambiguationData":[TD([[makeQuery(id+"F0.imprint","IMPRINT",EDGE,{"disambiguationData":[TD([[subQ2,-1.0]])],"derivedFrom":subQ1}),1.0]])]});}
            var Q58;
            {var subQ0=sQuery(id+"F0.wireOp",EDGE,"E29.MirrorC");var subQ2=sQuery(id+"F0.wireOp",EDGE,"E24");var subQ3=makeQuery(id+"F0.imprint","INTERSECT",VERTEX,{"disambiguationData":[OD(0.0)],"derivedFrom":[subQ2,subQ0]});Q58=makeQuery(id+"F0.imprint","IMPRINT",FACE,{"disambiguationData":[TD([[makeQuery(id+"F0.imprint","IMPRINT",EDGE,{"disambiguationData":[TD([[subQ3,-1.0]])],"derivedFrom":subQ2}),-1.0]])]});}
            var Q59;
            {var subQ0=sQuery(id+"F0.wireOp",EDGE,"E29.MirrorC");var subQ1=sQuery(id+"F0.wireOp",EDGE,"E24");var subQ2=makeQuery(id+"F0.imprint","INTERSECT",VERTEX,{"disambiguationData":[OD(0.0)],"derivedFrom":[subQ1,subQ0]});Q59=makeQuery(id+"F0.imprint","IMPRINT",FACE,{"disambiguationData":[TD([[makeQuery(id+"F0.imprint","IMPRINT",EDGE,{"disambiguationData":[TD([[subQ2,-1.0]])],"derivedFrom":subQ1}),1.0]])]});}
            var Q60;
            {var subQ0=sQuery(id+"F0.wireOp",EDGE,"E9");var subQ1=sQuery(id+"F0.wireOp",EDGE,"E2.left");var subQ2=makeQuery(id+"F0.imprint","INTERSECT",VERTEX,{"disambiguationData":[OD(1.0)],"derivedFrom":[subQ1,subQ0]});Q60=makeQuery(id+"F0.imprint","IMPRINT",FACE,{"disambiguationData":[TD([[makeQuery(id+"F0.imprint","IMPRINT",EDGE,{"disambiguationData":[TD([[subQ2,-1.0]])],"derivedFrom":subQ1}),1.0]])]});}
            var Q61;
            {var subQ0=sQuery(id+"F0.wireOp",EDGE,"E6");var subQ1=sQuery(id+"F0.wireOp",EDGE,"E2.left");var subQ2=makeQuery(id+"F0.imprint","INTERSECT",VERTEX,{"disambiguationData":[OD(1.0)],"derivedFrom":[subQ1,subQ0]});Q61=makeQuery(id+"F0.imprint","IMPRINT",FACE,{"disambiguationData":[TD([[makeQuery(id+"F0.imprint","IMPRINT",EDGE,{"disambiguationData":[TD([[subQ2,-1.0]])],"derivedFrom":subQ1}),1.0]])]});}
            var Q62;
            {var subQ0=sQuery(id+"F0.wireOp",EDGE,"E36");Q62=makeQuery(id+"F0.imprint","IMPRINT",FACE,{"disambiguationData":[TD([[makeQuery(id+"F0.imprint","IMPRINT",EDGE,{"derivedFrom":subQ0}),1.0]])]});}
            var Q63;
            {var subQ3=sQuery(id+"F0.wireOp",EDGE,"E32.left");Q63=makeQuery(id+"F0.imprint","IMPRINT",FACE,{"disambiguationData":[TD([[makeQuery(id+"F0.imprint","IMPRINT",EDGE,{"derivedFrom":subQ3}),1.0]])]});}
            var Q64;
            {var subQ0=sQuery(id+"F0.wireOp",EDGE,"E38");Q64=makeQuery(id+"F0.imprint","IMPRINT",FACE,{"disambiguationData":[TD([[makeQuery(id+"F0.imprint","IMPRINT",EDGE,{"derivedFrom":subQ0}),-1.0]])]});}
            var Q65;
            {var subQ0=sQuery(id+"F0.wireOp",EDGE,"E43.MirrorCS");Q65=makeQuery(id+"F0.imprint","IMPRINT",FACE,{"disambiguationData":[TD([[makeQuery(id+"F0.imprint","IMPRINT",EDGE,{"derivedFrom":subQ0}),-1.0]])]});}
            var Q66;
            {var subQ4=sQuery(id+"F0.wireOp",EDGE,"E42.MirrorCS");Q66=makeQuery(id+"F0.imprint","IMPRINT",FACE,{"disambiguationData":[TD([[makeQuery(id+"F0.imprint","IMPRINT",EDGE,{"derivedFrom":subQ4}),1.0]])]});}
            var Q67;
            {var subQ0=sQuery(id+"F0.wireOp",EDGE,"E45.MirrorCS");Q67=makeQuery(id+"F0.imprint","IMPRINT",FACE,{"disambiguationData":[TD([[makeQuery(id+"F0.imprint","IMPRINT",EDGE,{"derivedFrom":subQ0}),1.0]])]});}
            var Q68;
            {var subQ0=sQuery(id+"F0.wireOp",EDGE,"E24");var subQ1=sQuery(id+"F0.wireOp",EDGE,"E13.bottom");var subQ2=makeQuery(id+"F0.imprint","INTERSECT",VERTEX,{"disambiguationData":[OD(0.0)],"derivedFrom":[subQ1,subQ0]});Q68=makeQuery(id+"F0.imprint","IMPRINT",FACE,{"disambiguationData":[TD([[makeQuery(id+"F0.imprint","IMPRINT",EDGE,{"disambiguationData":[TD([[subQ2,-1.0]])],"derivedFrom":subQ1}),-1.0]])]});}
            var Q69;
            {var subQ0=sQuery(id+"F0.wireOp",EDGE,"E15.left");var subQ5=sQuery(id+"F0.wireOp",EDGE,"E22.1.0.0");var subQ6=makeQuery(id+"F0.imprint","INTERSECT",VERTEX,{"disambiguationData":[OD(0.0)],"derivedFrom":[subQ0,subQ5]});Q69=makeQuery(id+"F0.imprint","IMPRINT",FACE,{"disambiguationData":[TD([[makeQuery(id+"F0.imprint","IMPRINT",EDGE,{"disambiguationData":[TD([[subQ6,1.0]])],"derivedFrom":subQ5}),-1.0]])]});}
            var Q70;
            {var subQ0=sQuery(id+"F0.wireOp",EDGE,"E19");var subQ1=sQuery(id+"F0.wireOp",EDGE,"E13.bottom");var subQ2=makeQuery(id+"F0.imprint","INTERSECT",VERTEX,{"disambiguationData":[OD(1.0)],"derivedFrom":[subQ1,subQ0]});Q70=makeQuery(id+"F0.imprint","IMPRINT",FACE,{"disambiguationData":[TD([[makeQuery(id+"F0.imprint","IMPRINT",EDGE,{"disambiguationData":[TD([[subQ2,-1.0]])],"derivedFrom":subQ1}),-1.0]])]});}
            var Q71;
            {var subQ0=sQuery(id+"F0.wireOp",EDGE,"E14.left");var subQ5=sQuery(id+"F0.wireOp",EDGE,"E19");var subQ6=makeQuery(id+"F0.imprint","INTERSECT",VERTEX,{"disambiguationData":[OD(0.0)],"derivedFrom":[subQ0,subQ5]});Q71=makeQuery(id+"F0.imprint","IMPRINT",FACE,{"disambiguationData":[TD([[makeQuery(id+"F0.imprint","IMPRINT",EDGE,{"disambiguationData":[TD([[subQ6,-1.0]])],"derivedFrom":subQ5}),-1.0]])]});}
            extrude(context, id + "F1", {"entities" : qUnion([Q0, Q1, Q2, Q3, Q4, Q5, Q6, Q7, Q8, Q9, Q10, Q11, Q12, Q13, Q14, Q15, Q16, Q17, Q18, Q19, Q20, Q21, Q22, Q23, Q24, Q25, Q26, Q27, Q28, Q29, Q30, Q31, Q32, Q33, Q34, Q35, Q36, Q37, Q38, Q39, Q40, Q41, Q42, Q43, Q44, Q45, Q46, Q47, Q48, Q49, Q50, Q51, Q52, Q53, Q54, Q55, Q56, Q57, Q58, Q59, Q60, Q61, Q62, Q63, Q64, Q65, Q66, Q67, Q68, Q69, Q70, Q71]), "depth" : 5 * mm});
        }
    });
